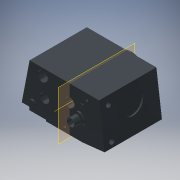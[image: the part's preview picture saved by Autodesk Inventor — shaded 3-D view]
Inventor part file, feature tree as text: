
AUTODESK INVENTOR PART (.ipt)
format: ipt  version: 2018 (Build 220112000, 112)  size: 353,792 bytes
history: native  units: in
note: dims shown in document units (in); Inventor stores cm internally (conversion verified against a paired STEP export)
features: sketch x18, extrude x17, fillet x2, thread x2, chamfer x1, hole x1, plane x1, other x1
ambient origin geometry x8: Origin, YZ Plane, XZ Plane, XY Plane, X Axis, Y Axis, Z Axis, Center Point
bodies: Solid1 (feature_tree)
feature tree (43):
  extrude  "Extrusion1"  Depth=10.4921in
  sketch  "Sketch3"  dims[d7=10.0in d8=0.5669in]
  extrude  "Extrusion2"  Depth=0.5669in
  extrude  "Extrusion3"  Depth=0.694in
  extrude  "Extrusion4"  Depth=0.7087in
  extrude  "Extrusion5"  Depth=0.0787in
  extrude  "Extrusion6"  Depth=13.4646in TaperAngle=0.0deg
  fillet  "Fillet1"  Radius=5.5118in
  fillet  "Fillet2"  Radius=6.2992in
  extrude  "Extrusion7"  Depth=2.7559in
  thread  "Thread1"  [1 undecoded]
  extrude  "Extrusion8"  Depth=1.1811in
  extrude  "Extrusion9"  Depth=1.7717in
  extrude  "Extrusion10"  Depth=1.2106in
  chamfer  "Chamfer1"  Distance=2.3622in
  extrude  "Extrusion11"  Depth=0.748in
  extrude  "Extrusion12"  Depth=1.0236in TaperAngle=0.0deg
  extrude  "Extrusion13"  Depth=1.0236in TaperAngle=0.0deg
  extrude  "Extrusion14"  Depth=1.378in
  hole  "Hole1"  [1 undecoded]
  extrude  "Extrusion15"  Depth=0.0787in
  extrude  "Extrusion16"  Depth=0.7874in
  extrude  "Extrusion17"  Depth=1.1811in TaperAngle=0.0deg
  thread  "Thread2"  [1 undecoded]
  plane  "Work Plane2"
  sketch  "Sketch1"  dims[d0=8.6614in d1=10.4921in]
  sketch  "Sketch4"  dims[d9=9.6457in d10=0.694in]
  sketch  "Sketch5"  dims[d11=1.7717in d12=0.7087in]
  sketch  "Sketch6"  dims[d14=16.3386in d15=0.0787in]
  sketch  "Sketch7"  dims[d16=0.0787in d17=13.4646in d18=0.0in d22=5.5118in d26=6.2992in]
  sketch  "Sketch8"  dims[d27=2.7559in d28=3.6024in d29=2.7559in]
  sketch  "Sketch10"  dims[d30=0.3937in d31=0.0in d34=1.1811in]
  sketch  "Sketch11"  dims[d37=1.7717in d38=2.0079in]
  sketch  "Sketch12"  dims[d39=1.2402in d42=1.2106in]
  sketch  "Sketch13"  dims[d43=1.8799in d44=2.3622in d45=0.0in]
  sketch  "Sketch14"  dims[d49=6.3386in d50=0.748in]
  sketch  "Sketch15"  dims[d52=7.4213in d53=1.0236in d54=0.0in]
  sketch  "Sketch16"  dims[d55=2.2835in d56=1.0236in d57=0.0in]
  sketch  "Sketch17"  dims[d69=0.7874in d70=1.378in]
  sketch  "Sketch19"  dims[d72=0.3937in d73=0.315in]
  sketch  "Sketch20"  dims[d75=0.2362in d76=0.0in d77=0.0787in]
  sketch  "Sketch21"  dims[d78=0.0787in d82=0.7874in d83=1.1811in d84=0.0in d85=0.3937in d86=0.0in d87=3.0118in d88=45.0deg d91=0.3937in d92=0.0in d93=2.0079in d94=1.6929in d95=1.4961in d96=0.0in d97=1.9685in d98=0.0in d99=0.0787in d100=0.0787in d101=45.0deg d103=1.1811in d105=0.3937in d106=0.0in d107=5.9055in d108=5.9646in d109=90.0deg d110=2.7559in d111=7.4803in d112=90.0deg d113=0.3937in d114=0.0in d116=0.3937in d117=0.0in d118=2.9528in d120=3.2283in d121=1.1811in d122=0.1969in d123=0.0in d124=0.2559in d125=0.1181in d126=0.2362in d127=0.2559in d128=0.0787in d129=90.0deg d130=0.1969in d131=0.0in d132=6.6929in d133=90.0deg d134=1.7323in d135=2.4409in d136=0.7874in d137=0.0in d138=5.9055in d139=5.9646in d140=90.0deg d141=2.1654in d142=2.7559in d143=0.0in d144=0.9843in d145=1.3386in d146=0.7874in d147=0.7874in d148=0.0in d149=0.3937in d150=0.0in d151=0.0in]
  other  "Work Axis1"
note: 3 required parameter values undecoded (feature->parameter linkage not recoverable at this tier; creation-order binding heuristic only, values carry confidence <= 0.55)
